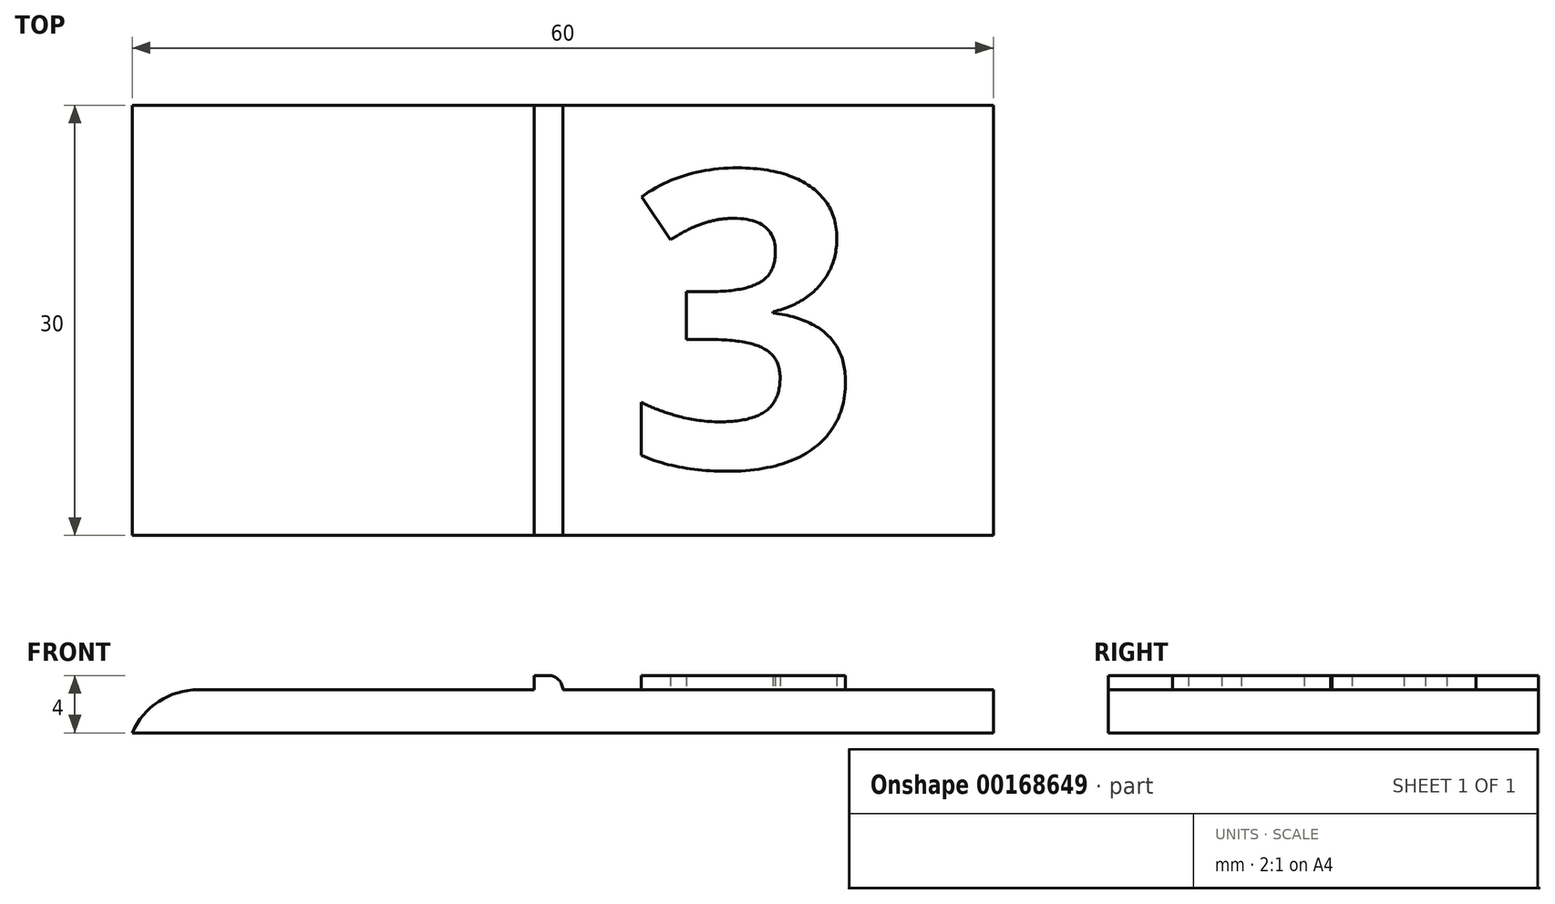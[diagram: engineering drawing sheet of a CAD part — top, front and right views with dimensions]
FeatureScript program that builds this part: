
annotation { "Feature Type Name" : "Feature", "Feature Type Description" : "" }
export const myFeature = defineFeature(function(context is Context, id is Id, definition is map)
    precondition{}
    {
        {
            var Q0;
            Q0=qCreatedBy(makeId("Top.planeOp"),FACE);
            var sketch = newSketch(context, id + "F0", { "sketchPlane" : qUnion([Q0])});
            skLineSegment(sketch, "E0.bottom", {"start": v(0, 0) * mm, "end": v(60, 0) * mm});
            skLineSegment(sketch, "E0.top", {"start": v(0, 30) * mm, "end": v(60, 30) * mm});
            skLineSegment(sketch, "E0.left", {"start": v(0, 0) * mm, "end": v(0, 30) * mm});
            skLineSegment(sketch, "E0.right", {"start": v(60, 0) * mm, "end": v(60, 30) * mm});
            skSolve(sketch);
        }
        {
            var Q0;
            Q0=qSketchRegion(id+"F0",true);
            extrude(context, id + "F1", {"entities" : qUnion([Q0]), "depth" : 3 * mm});
        }
        {
            var Q0;
            Q0=makeQuery(id+"F1.opExtrude","CAP_FACE",FACE,{"disambiguationData":[OSD([sQuery(id+"F0.wireOp",EDGE,"E0.bottom"),sQuery(id+"F0.wireOp",EDGE,"E0.top"),sQuery(id+"F0.wireOp",EDGE,"E0.left"),sQuery(id+"F0.wireOp",EDGE,"E0.right")])],"isStart":false});
            var sketch = newSketch(context, id + "F2", { "sketchPlane" : qUnion([Q0])});
            skLineSegment(sketch, "E1.bottom", {"start": v(30, 30) * mm, "end": v(28, 30) * mm});
            skLineSegment(sketch, "E1.top", {"start": v(30, 0) * mm, "end": v(28, 0) * mm});
            skLineSegment(sketch, "E1.left", {"start": v(30, 30) * mm, "end": v(30, 0) * mm});
            skLineSegment(sketch, "E1.right", {"start": v(28, 30) * mm, "end": v(28, 0) * mm});
            skSolve(sketch);
        }
        {
            var Q0;
            Q0=qSketchRegion(id+"F2",true);
            extrude(context, id + "F3", {"entities" : qUnion([Q0]), "operationType" : NewBodyOperationType.ADD, "depth" : 1 * mm});
        }
        {
            var Q0;
            Q0=makeQuery(id+"F3.opExtrude","CAP_EDGE",EDGE,{"disambiguationData":[OSD([sQuery(id+"F2.wireOp",EDGE,"E1.left")])],"isStart":false});
            fillet(context, id + "F4", {"entities" : qUnion([Q0]), "radius" : 1 * mm, "tangentPropagation" : true, "allowEdgeOverflow" : false});
        }
        {
            var Q0;
            {var subQ0=sQuery(id+"F0.wireOp",EDGE,"E0.top");var subQ1=sQuery(id+"F0.wireOp",EDGE,"E0.right");var subQ2=sQuery(id+"F0.wireOp",EDGE,"E0.bottom");Q0=makeQuery(id+"F3.boolean.opBoolean","SPLIT",FACE,{"disambiguationData":[TD([makeQuery(id+"F1.opExtrude","SWEPT_FACE",FACE,{"disambiguationData":[OSD([subQ1])]})])],"derivedFrom":makeQuery(id+"F1.opExtrude","CAP_FACE",FACE,{"disambiguationData":[OSD([subQ2,subQ0,sQuery(id+"F0.wireOp",EDGE,"E0.left"),subQ1])],"isStart":false})});}
            var sketch = newSketch(context, id + "F5", { "sketchPlane" : qUnion([Q0])});
            skText(sketch, "E2", { "text": "3\n", "fontName": "OpenSans-Bold.ttf"});
            const initialGuessF5  = {"E2": [0.03436, 0.00476, 1, 0, 0.02075]};
            skSetInitialGuess(sketch, initialGuessF5);
            skSolve(sketch);
        }
        {
            var Q0;
            Q0=qSketchRegion(id+"F5",true);
            extrude(context, id + "F6", {"entities" : qUnion([Q0]), "operationType" : NewBodyOperationType.ADD, "depth" : 1 * mm});
        }
        {
            var Q0;
            Q0=makeQuery(id+"F1.opExtrude","CAP_EDGE",EDGE,{"disambiguationData":[OSD([sQuery(id+"F0.wireOp",EDGE,"E0.left")])],"isStart":false});
            fillet(context, id + "F7", {"entities" : qUnion([Q0]), "radius" : 5 * mm, "tangentPropagation" : true, "allowEdgeOverflow" : false});
        }
    });
